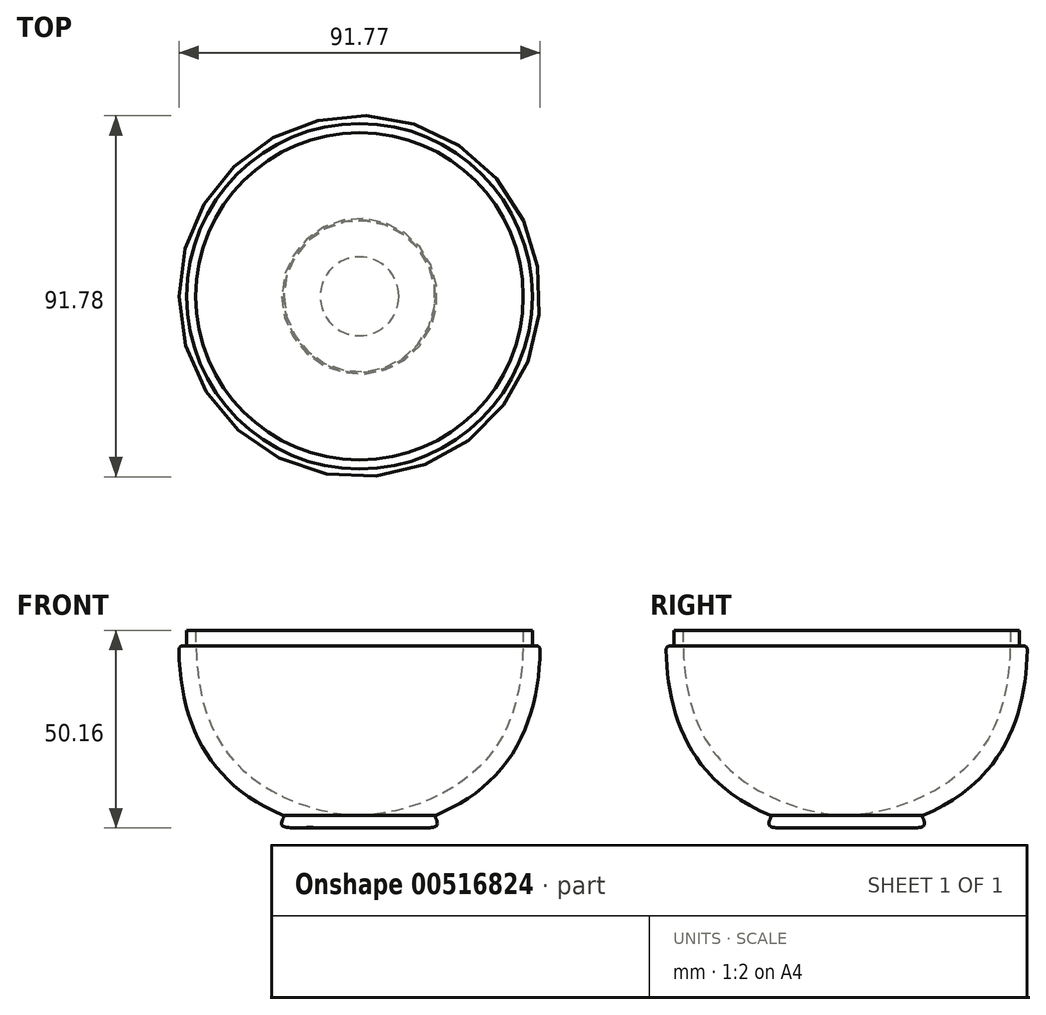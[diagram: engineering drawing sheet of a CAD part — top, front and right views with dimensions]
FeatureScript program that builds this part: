
annotation { "Feature Type Name" : "Feature", "Feature Type Description" : "" }
export const myFeature = defineFeature(function(context is Context, id is Id, definition is map)
    precondition{}
    {
        {
            var Q0;
            Q0=qCreatedBy(makeId("Front.planeOp"),FACE);
            var sketch = newSketch(context, id + "F0", { "sketchPlane" : qUnion([Q0])});
            skLineSegment(sketch, "E0", {"start": v(9.26, -31.93) * mm, "end": v(-0.74, -31.93) * mm, "construction": true});
            skLineSegment(sketch, "E1", {"start": v(-32.34, 18.2) * mm, "end": v(-34.64, 18.2) * mm});
            skLineSegment(sketch, "E2", {"start": v(-34.64, 18.2) * mm, "end": v(-34.64, 14.27) * mm});
            skLineSegment(sketch, "E3", {"start": v(-34.64, 14.27) * mm, "end": v(-36.64, 14.27) * mm});
            skLineSegment(sketch, "E4", {"start": v(9.26, -31.93) * mm, "end": v(-0.74, -31.93) * mm});
            skLineSegment(sketch, "E5", {"start": v(9.26, -31.93) * mm, "end": v(9.26, -28.93) * mm});
            skFitSpline(sketch, "E6", {"points": [v(-36.64, 14.27) * mm, v(-28.86, -14.2) * mm, v(-0.74, -31.93) * mm], "startDerivative": vector(0.49, -69.86) * mm, "endDerivative": vector(80.58, -21.17) * mm});
            skLineSegment(sketch, "E7", {"start": v(9.16, 19.07) * mm, "end": v(9.26, -28.93) * mm, "construction": true});
            skFitSpline(sketch, "E8", {"points": [v(-32.34, 18.2) * mm, v(-23.85, -13.53) * mm, v(9.26, -28.93) * mm], "startDerivative": vector(-0.65, -77.78) * mm, "endDerivative": vector(80.9, -4.74) * mm});
            skLineSegment(sketch, "E9", {"start": v(9.16, 19.07) * mm, "end": v(9.26, -28.88) * mm, "construction": true});
            skFitSpline(sketch, "E10", {"points": [v(-0.74, -31.93) * mm, v(-4.58, -31.93) * mm, v(-8.63, -31.93) * mm, v(-10.5, -31.09) * mm, v(-9.95, -28.86) * mm, v(-10.06, -28.82) * mm, v(-10.12, -28.79) * mm], "startDerivative": vector(-14.5, 0.48) * mm, "endDerivative": vector(-1.56, 0.97) * mm});
            skSolve(sketch);
        }
        {
            var Q0;
            Q0=makeQuery(id+"F0.imprint","IMPRINT",FACE,{"disambiguationData":[TD([[makeQuery(id+"F0.imprint","IMPRINT",EDGE,{"derivedFrom":sQuery(id+"F0.wireOp",EDGE,"E1")}),1.0]])]});
            var Q1;
            {var subQ0=sQuery(id+"F0.wireOp",EDGE,"E10");var subQ1=sQuery(id+"F0.wireOp",EDGE,"E6");var subQ3=makeQuery(id+"F0.imprint","INTERSECT",VERTEX,{"disambiguationData":[OD(2.0)],"derivedFrom":[subQ1,subQ0]});Q1=makeQuery(id+"F0.imprint","IMPRINT",FACE,{"disambiguationData":[TD([[makeQuery(id+"F0.imprint","IMPRINT",EDGE,{"disambiguationData":[TD([[subQ3,-1.0]])],"derivedFrom":subQ1}),-1.0]])]});}
            var Q2;
            Q2=sQuery(id+"F0.wireOp",EDGE,"E5");
            revolve(context, id + "F1", {"entities" : qUnion([Q0, Q1]), "axis" : qUnion([Q2]), "revolveType" : RevolveType.FULL});
        }
        {
            var Q0;
            Q0=makeQuery(id+"F1.opRevolve","SWEPT_EDGE",EDGE,{"disambiguationData":[OSD([sQuery(id+"F0.wireOp",EDGE,"E3"),sQuery(id+"F0.wireOp",EDGE,"E6")])]});
            fillet(context, id + "F2", {"entities" : qUnion([Q0]), "radius" : 1 * mm, "tangentPropagation" : true, "allowEdgeOverflow" : false});
        }
    });
